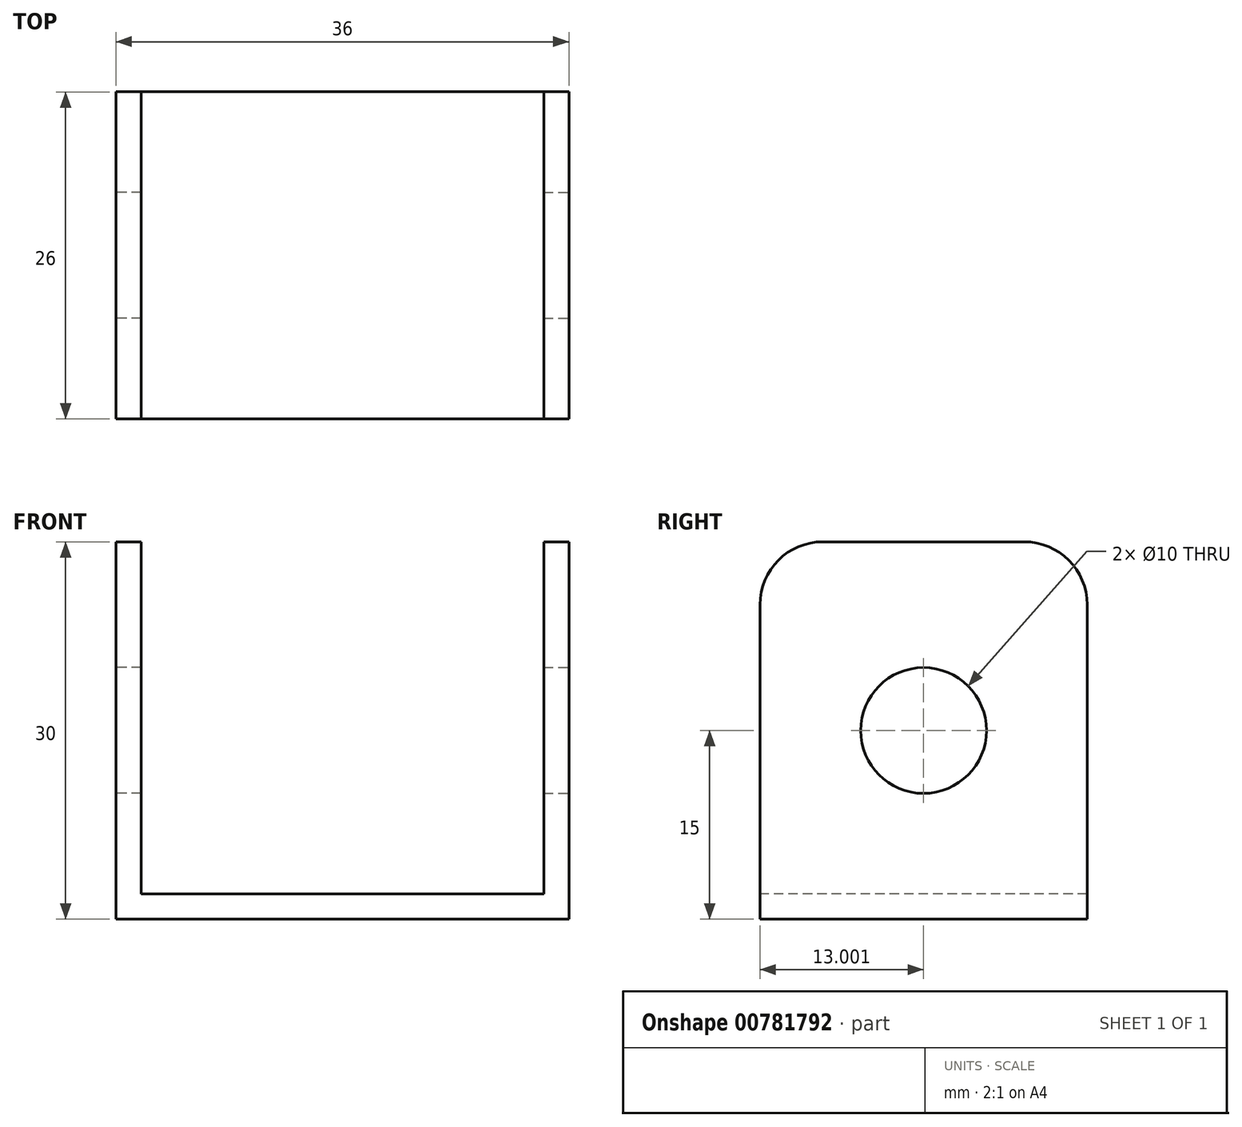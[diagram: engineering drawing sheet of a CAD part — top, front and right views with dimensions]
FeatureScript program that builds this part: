
annotation { "Feature Type Name" : "Feature", "Feature Type Description" : "" }
export const myFeature = defineFeature(function(context is Context, id is Id, definition is map)
    precondition{}
    {
        {
            var Q0;
            Q0=qCreatedBy(makeId("Top.planeOp"),FACE);
            var sketch = newSketch(context, id + "F0", { "sketchPlane" : qUnion([Q0])});
            skLineSegment(sketch, "E0.top", {"start": v(0, 18.4) * mm, "end": v(-18, 18.4) * mm});
            skLineSegment(sketch, "E0.left", {"start": v(0, 0) * mm, "end": v(0, 18.4) * mm});
            skLineSegment(sketch, "E1.top", {"start": v(0, -7.6) * mm, "end": v(-18, -7.6) * mm});
            skLineSegment(sketch, "E1.left", {"start": v(0, 0) * mm, "end": v(0, -7.6) * mm});
            skLineSegment(sketch, "E2", {"start": v(-18, 18.4) * mm, "end": v(-18, -7.6) * mm});
            skLineSegment(sketch, "E3", {"start": v(-16, 18.4) * mm, "end": v(-16, -7.6) * mm});
            skSolve(sketch);
        }
        {
            var Q0;
            {var subQ3=sQuery(id+"F0.wireOp",EDGE,"E0.left");Q0=makeQuery(id+"F0.imprint","IMPRINT",FACE,{"disambiguationData":[TD([[makeQuery(id+"F0.imprint","IMPRINT",EDGE,{"derivedFrom":subQ3}),1.0]])]});}
            extrude(context, id + "F1", {"entities" : qUnion([Q0]), "depth" : 2 * mm, "offsetDistance" : 25 * mm});
        }
        {
            var Q0;
            {var subQ0=sQuery(id+"F0.wireOp",EDGE,"E2");Q0=makeQuery(id+"F0.imprint","IMPRINT",FACE,{"disambiguationData":[TD([[makeQuery(id+"F0.imprint","IMPRINT",EDGE,{"derivedFrom":subQ0}),1.0]])]});}
            extrude(context, id + "F2", {"entities" : qUnion([Q0]), "operationType" : NewBodyOperationType.ADD, "depth" : 30 * mm, "offsetDistance" : 25 * mm});
        }
        {
            var Q0;
            Q0=makeQuery(id+"F2.opExtrude","SWEPT_FACE",FACE,{"disambiguationData":[OSD([sQuery(id+"F0.wireOp",EDGE,"E2")])]});
            var sketch = newSketch(context, id + "F3", { "sketchPlane" : qUnion([Q0])});
            skCircle(sketch, "E4", {"center": v(-5.4, 15) * mm, "radius": 5 * mm});
            skSolve(sketch);
        }
        {
            var Q0;
            Q0=makeQuery(id+"F3.imprint","IMPRINT",FACE,{"disambiguationData":[TD([[makeQuery(id+"F3.imprint","IMPRINT",EDGE,{"derivedFrom":sQuery(id+"F3.wireOp",EDGE,"E4")}),1.0]])]});
            extrude(context, id + "F4", {"entities" : qUnion([Q0]), "operationType" : NewBodyOperationType.REMOVE, "oppositeDirection" : true, "depth" : 2 * mm, "offsetDistance" : 25 * mm});
        }
        {
            var Q0;
            Q0=makeQuery(id+"F2.opExtrude","CAP_EDGE",EDGE,{"disambiguationData":[OSD([sQuery(id+"F0.wireOp",EDGE,"E0.top")])],"isStart":false});
            var Q1;
            Q1=makeQuery(id+"F2.opExtrude","CAP_EDGE",EDGE,{"disambiguationData":[OSD([sQuery(id+"F0.wireOp",EDGE,"E1.top")])],"isStart":false});
            fillet(context, id + "F5", {"entities" : qUnion([Q0, Q1]), "radius" : 5 * mm, "tangentPropagation" : true, "allowEdgeOverflow" : false});
        }
        {
            var Q0;
            Q0=makeQuery(id+"F1.opExtrude","SWEPT_BODY",BODY,{"disambiguationData":[OSD([sQuery(id+"F0.wireOp",EDGE,"E0.top"),sQuery(id+"F0.wireOp",EDGE,"E0.left"),sQuery(id+"F0.wireOp",EDGE,"E1.top"),sQuery(id+"F0.wireOp",EDGE,"E1.left"),sQuery(id+"F0.wireOp",EDGE,"E3")])]});
            var Q1;
            Q1=qCreatedBy(makeId("Right.planeOp"),FACE);
            mirror(context, id + "F6", {"operationType" : NewBodyOperationType.ADD, "entities" : qUnion([Q0]), "mirrorPlane" : qUnion([Q1])});
        }
    });
